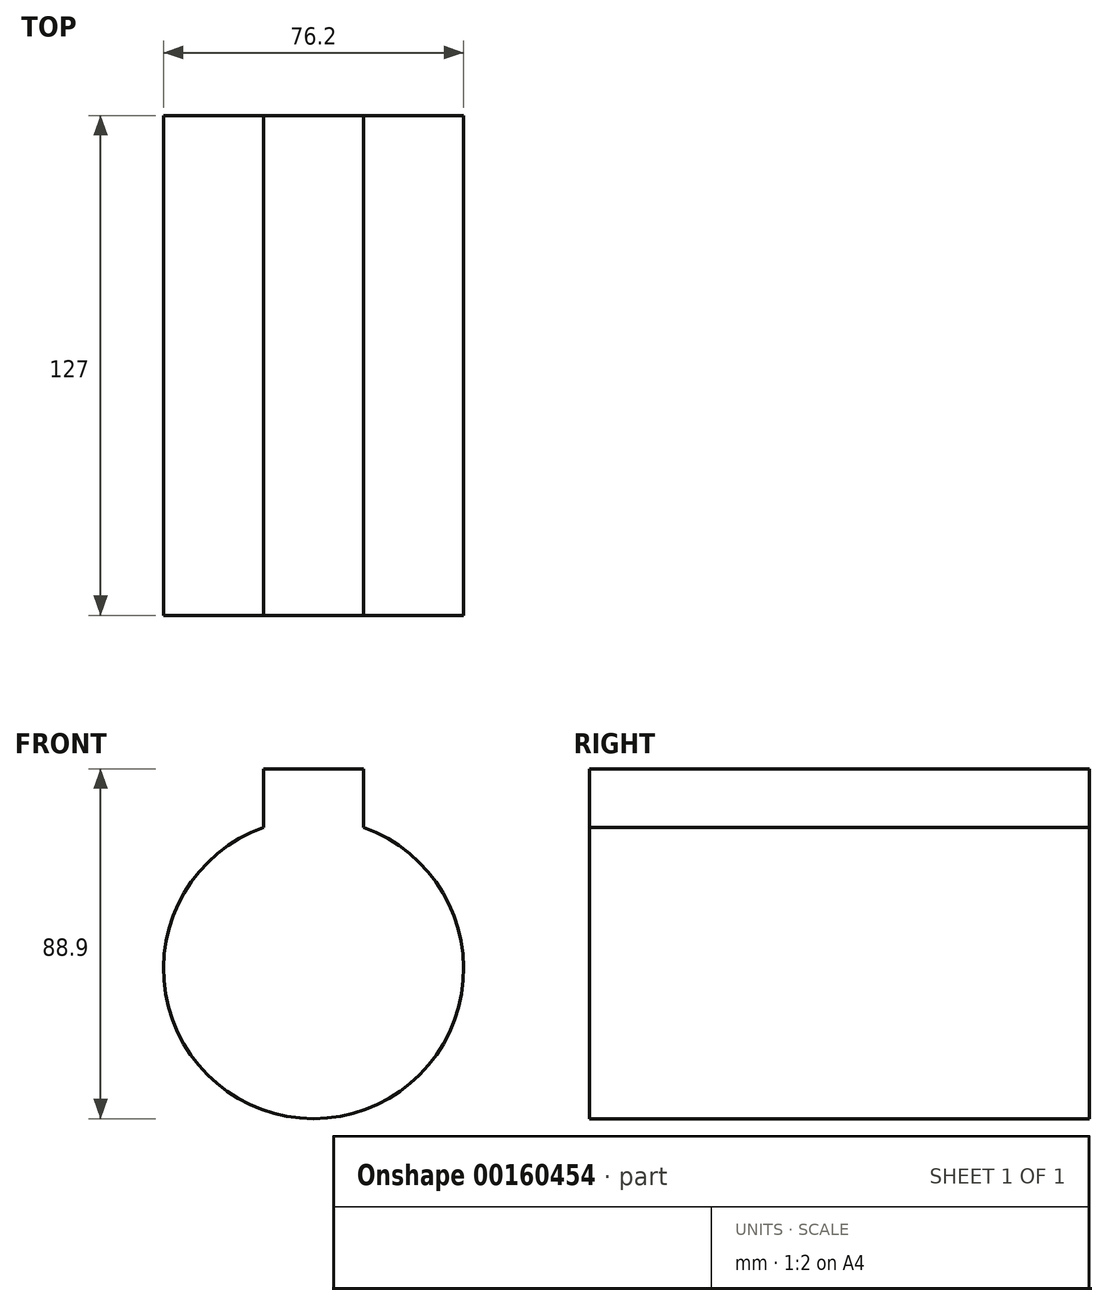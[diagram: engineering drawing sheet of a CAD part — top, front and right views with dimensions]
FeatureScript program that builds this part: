
annotation { "Feature Type Name" : "Feature", "Feature Type Description" : "" }
export const myFeature = defineFeature(function(context is Context, id is Id, definition is map)
    precondition{}
    {
        {
            var Q0;
            Q0=qCreatedBy(makeId("Front.planeOp"),FACE);
            var sketch = newSketch(context, id + "F0", { "sketchPlane" : qUnion([Q0])});
            skArc(sketch, "E0", {"start": v(-12.7, 35.92) * mm, "mid": v(0, -38.1) * mm, "end": v(12.7, 35.92) * mm});
            skLineSegment(sketch, "E1.bottom", {"start": v(-12.7, 50.8) * mm, "end": v(12.7, 50.8) * mm});
            skLineSegment(sketch, "E1.left", {"start": v(-12.7, 50.8) * mm, "end": v(-12.7, 35.92) * mm});
            skLineSegment(sketch, "E1.right", {"start": v(12.7, 50.8) * mm, "end": v(12.7, 35.92) * mm});
            skSolve(sketch);
        }
        {
            var Q0;
            Q0=makeQuery(id+"F0.imprint","IMPRINT",FACE,{"disambiguationData":[TD([[makeQuery(id+"F0.imprint","IMPRINT",EDGE,{"derivedFrom":sQuery(id+"F0.wireOp",EDGE,"E0")}),1.0]])]});
            extrude(context, id + "F1", {"entities" : qUnion([Q0]), "depth" : 127 * mm});
        }
    });
